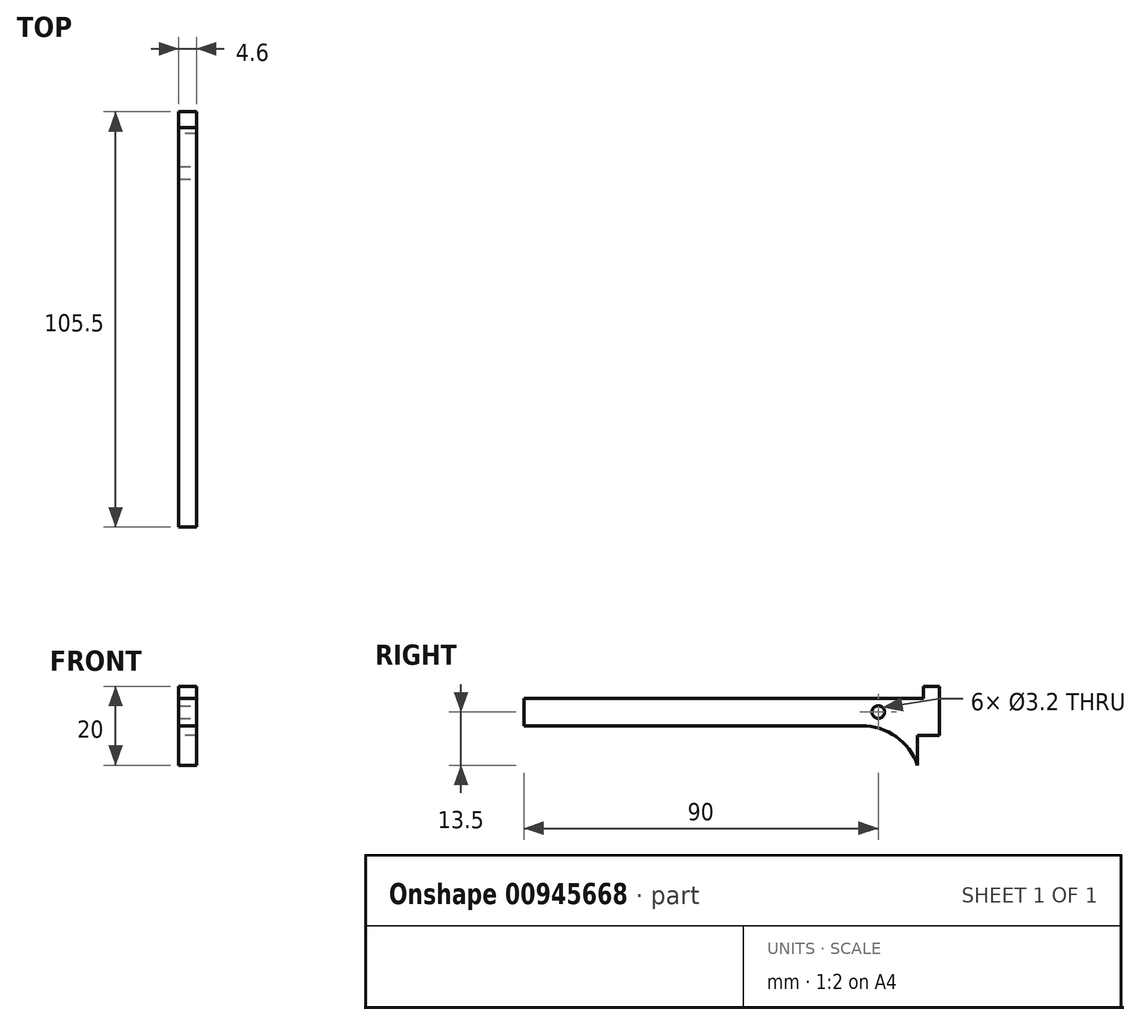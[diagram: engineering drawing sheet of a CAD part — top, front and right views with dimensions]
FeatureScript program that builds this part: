
annotation { "Feature Type Name" : "Feature", "Feature Type Description" : "" }
export const myFeature = defineFeature(function(context is Context, id is Id, definition is map)
    precondition{}
    {
        {
            var Q0;
            Q0=qCreatedBy(makeId("Right.planeOp"),FACE);
            var sketch = newSketch(context, id + "F0", { "sketchPlane" : qUnion([Q0])});
            skLineSegment(sketch, "E0", {"start": v(0, 0) * mm, "end": v(0, 7.5) * mm});
            skLineSegment(sketch, "E1", {"start": v(0, 7.5) * mm, "end": v(5.5, 7.5) * mm});
            skLineSegment(sketch, "E2", {"start": v(5.5, 7.5) * mm, "end": v(5.5, 20) * mm});
            skLineSegment(sketch, "E3", {"start": v(5.5, 20) * mm, "end": v(1.5, 20) * mm});
            skLineSegment(sketch, "E4", {"start": v(1.5, 20) * mm, "end": v(1.5, 17) * mm});
            skLineSegment(sketch, "E5", {"start": v(1.5, 17) * mm, "end": v(-100, 17) * mm});
            skLineSegment(sketch, "E6", {"start": v(-100, 17) * mm, "end": v(-100, 10) * mm});
            skLineSegment(sketch, "E7", {"start": v(-100, 10) * mm, "end": v(-14.14, 10) * mm});
            skArc(sketch, "E8", {"start": v(-14.14, 10) * mm, "mid": v(-5.48, 7.25) * mm, "end": v(0, 0) * mm});
            skPoint(sketch, "E9", {"position": v(-100, 13.5) * mm});
            skPoint(sketch, "E10", {"position": v(-10, 13.5) * mm});
            skSolve(sketch);
        }
        {
            var Q0;
            Q0=makeQuery(id+"F0.imprint","IMPRINT",FACE,{"disambiguationData":[TD([[makeQuery(id+"F0.imprint","IMPRINT",EDGE,{"derivedFrom":sQuery(id+"F0.wireOp",EDGE,"E0")}),1.0]])]});
            extrude(context, id + "F1", {"entities" : qUnion([Q0]), "endBound" : BoundingType.SYMMETRIC, "depth" : 4.6 * mm, "offsetDistance" : 25 * mm});
        }
        {
            var Q0;
            Q0=makeQuery(id+"F1.opExtrude","CAP_FACE",FACE,{"disambiguationData":[OSD([sQuery(id+"F0.wireOp",EDGE,"E0"),sQuery(id+"F0.wireOp",EDGE,"E1"),sQuery(id+"F0.wireOp",EDGE,"E2"),sQuery(id+"F0.wireOp",EDGE,"E3"),sQuery(id+"F0.wireOp",EDGE,"E4"),sQuery(id+"F0.wireOp",EDGE,"E5"),sQuery(id+"F0.wireOp",EDGE,"E6"),sQuery(id+"F0.wireOp",EDGE,"E7"),sQuery(id+"F0.wireOp",EDGE,"E8")])],"isStart":false});
            var sketch = newSketch(context, id + "F2", { "sketchPlane" : qUnion([Q0])});
            skPoint(sketch, "E11", {"position": v(-10, 13.5) * mm});
            skSolve(sketch);
        }
        {
            var Q0;
            Q0=sQuery(id+"F2.wireOp",VERTEX,"E11");
            var Q1;
            Q1=makeQuery(id+"F1.opExtrude","SWEPT_BODY",BODY,{"disambiguationData":[OSD([sQuery(id+"F0.wireOp",EDGE,"E0"),sQuery(id+"F0.wireOp",EDGE,"E1"),sQuery(id+"F0.wireOp",EDGE,"E2"),sQuery(id+"F0.wireOp",EDGE,"E3"),sQuery(id+"F0.wireOp",EDGE,"E4"),sQuery(id+"F0.wireOp",EDGE,"E5"),sQuery(id+"F0.wireOp",EDGE,"E6"),sQuery(id+"F0.wireOp",EDGE,"E7"),sQuery(id+"F0.wireOp",EDGE,"E8")])]});
            hole(context, id + "F3", {"style" : HoleStyle.SIMPLE, "endStyle" : HoleEndStyle.THROUGH, "holeDiameter" : 3.2 * mm, "majorDiameter" : 3 * mm, "isTappedThrough" : true, "tappedDepth" : 12 * mm, "tapClearance" : 3, "locations" : qUnion([Q0]), "scope" : qUnion([Q1])});
        }
    });
